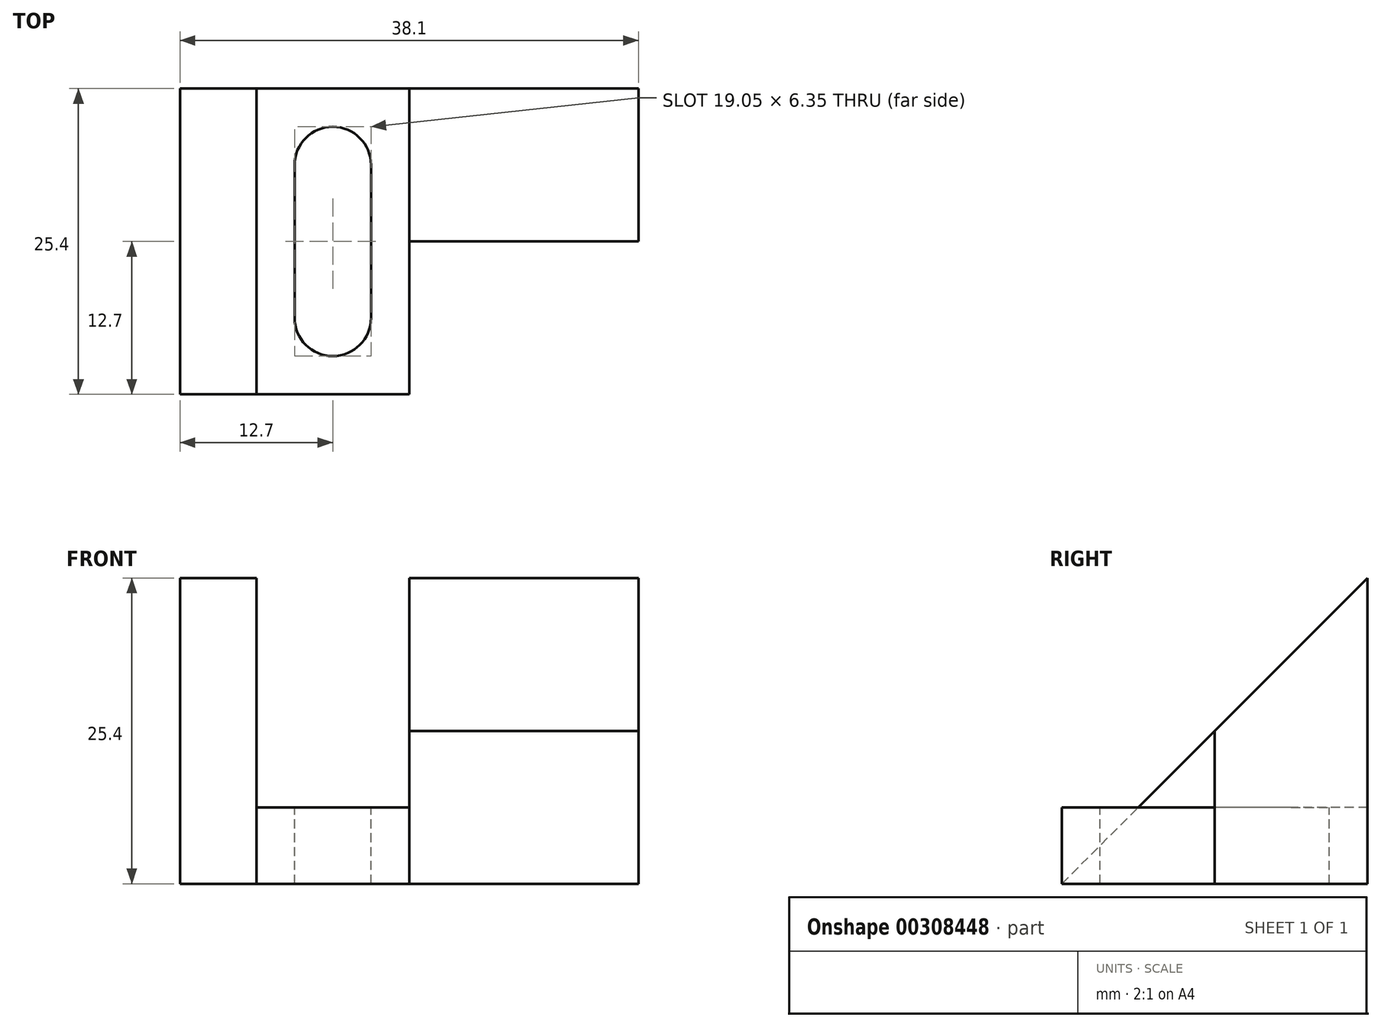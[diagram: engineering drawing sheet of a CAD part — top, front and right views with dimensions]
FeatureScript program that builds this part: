
annotation { "Feature Type Name" : "Feature", "Feature Type Description" : "" }
export const myFeature = defineFeature(function(context is Context, id is Id, definition is map)
    precondition{}
    {
        {
            var Q0;
            Q0=qCreatedBy(makeId("Right.planeOp"),FACE);
            var sketch = newSketch(context, id + "F0", { "sketchPlane" : qUnion([Q0])});
            skLineSegment(sketch, "E0", {"start": v(0, 0) * mm, "end": v(25.4, 25.4) * mm});
            skLineSegment(sketch, "E1", {"start": v(25.4, 25.4) * mm, "end": v(25.4, 0) * mm});
            skLineSegment(sketch, "E2", {"start": v(25.4, 0) * mm, "end": v(0, 0) * mm});
            skLineSegment(sketch, "E3", {"start": v(25.4, 6.35) * mm, "end": v(0, 6.35) * mm});
            skLineSegment(sketch, "E4", {"start": v(0, 6.35) * mm, "end": v(0, 0) * mm});
            skLineSegment(sketch, "E5", {"start": v(12.7, 12.7) * mm, "end": v(12.7, 0) * mm});
            skSolve(sketch);
        }
        {
            var Q0;
            {var subQ0=sQuery(id+"F0.wireOp",EDGE,"E1");var subQ1=sQuery(id+"F0.wireOp",EDGE,"E0");var subQ2=makeQuery(id+"F0.imprint","INTERSECT",VERTEX,{"derivedFrom":[subQ1,subQ0]});Q0=makeQuery(id+"F0.imprint","IMPRINT",FACE,{"disambiguationData":[TD([[makeQuery(id+"F0.imprint","IMPRINT",EDGE,{"disambiguationData":[TD([[subQ2,1.0]])],"derivedFrom":subQ1}),-1.0]])]});}
            var Q1;
            {var subQ0=sQuery(id+"F0.wireOp",EDGE,"E2");Q1=makeQuery(id+"F0.imprint","IMPRINT",FACE,{"disambiguationData":[TD([[makeQuery(id+"F0.imprint","IMPRINT",EDGE,{"derivedFrom":subQ0}),-1.0]])]});}
            var Q2;
            {var subQ0=sQuery(id+"F0.wireOp",EDGE,"E5");var subQ1=sQuery(id+"F0.wireOp",EDGE,"E0");var subQ2=makeQuery(id+"F0.imprint","INTERSECT",VERTEX,{"derivedFrom":[subQ1,subQ0]});Q2=makeQuery(id+"F0.imprint","IMPRINT",FACE,{"disambiguationData":[TD([[makeQuery(id+"F0.imprint","IMPRINT",EDGE,{"disambiguationData":[TD([[subQ2,1.0]])],"derivedFrom":subQ1}),-1.0]])]});}
            extrude(context, id + "F1", {"entities" : qUnion([Q0, Q1, Q2]), "depth" : 6.35 * mm});
        }
        {
            var Q0;
            Q0=makeQuery(id+"F1.opExtrude","CAP_FACE",FACE,{"disambiguationData":[OSD([sQuery(id+"F0.wireOp",EDGE,"E0"),sQuery(id+"F0.wireOp",EDGE,"E1"),sQuery(id+"F0.wireOp",EDGE,"E2")])],"isStart":false});
            var sketch = newSketch(context, id + "F2", { "sketchPlane" : qUnion([Q0])});
            skLineSegment(sketch, "E6.0", {"start": v(25.4, 25.4) * mm, "end": v(25.4, 0) * mm});
            skLineSegment(sketch, "E7.0", {"start": v(25.4, 6.35) * mm, "end": v(0, 6.35) * mm});
            skLineSegment(sketch, "E8.0", {"start": v(0, 6.35) * mm, "end": v(0, 0) * mm});
            skLineSegment(sketch, "E9.0", {"start": v(25.4, 0) * mm, "end": v(0, 0) * mm});
            skSolve(sketch);
        }
        {
            var Q0;
            Q0 = qSketchRegion(id + "F2", true);
            extrude(context, id + "F3", {"entities" : qUnion([Q0]), "operationType" : NewBodyOperationType.ADD, "depth" : 12.7 * mm});
        }
        {
            var Q0;
            Q0=makeQuery(id+"F3.opExtrude","CAP_FACE",FACE,{"disambiguationData":[OSD([sQuery(id+"F2.wireOp",EDGE,"E6.0"),sQuery(id+"F2.wireOp",EDGE,"E7.0"),sQuery(id+"F2.wireOp",EDGE,"E8.0"),sQuery(id+"F2.wireOp",EDGE,"E9.0")])],"isStart":false});
            var sketch = newSketch(context, id + "F4", { "sketchPlane" : qUnion([Q0])});
            skLineSegment(sketch, "E10.0", {"start": v(12.7, 12.7) * mm, "end": v(12.7, 0) * mm});
            skLineSegment(sketch, "E11.0", {"start": v(25.4, 25.4) * mm, "end": v(25.4, 0) * mm});
            skLineSegment(sketch, "E12", {"start": v(25.4, 25.4) * mm, "end": v(12.7, 12.7) * mm});
            skLineSegment(sketch, "E13", {"start": v(12.7, 0) * mm, "end": v(25.4, 0) * mm});
            skSolve(sketch);
        }
        {
            var Q0;
            Q0 = qSketchRegion(id + "F4", true);
            extrude(context, id + "F5", {"entities" : qUnion([Q0]), "operationType" : NewBodyOperationType.ADD, "depth" : 19.05 * mm});
        }
        {
            var Q0;
            Q0=makeQuery(id+"F3.opExtrude","SWEPT_FACE",FACE,{"disambiguationData":[OSD([sQuery(id+"F2.wireOp",EDGE,"E7.0")])]});
            var sketch = newSketch(context, id + "F6", { "sketchPlane" : qUnion([Q0])});
            skLineSegment(sketch, "E14", {"start": v(12.7, 19.05) * mm, "end": v(12.7, 6.35) * mm, "construction": true});
            skPoint(sketch, "E14.startSnap0", {"position": v(19.05, 19.05) * mm});
            skPoint(sketch, "E14.startSnap1", {"position": v(12.7, 25.4) * mm});
            skPoint(sketch, "E14.endSnap0", {"position": v(12.7, 0) * mm});
            skArc(sketch, "E15.0.startCap", {"start": v(9.53, 19.05) * mm, "mid": v(12.7, 22.23) * mm, "end": v(15.88, 19.05) * mm});
            skArc(sketch, "E15.0.endCap", {"start": v(15.88, 6.35) * mm, "mid": v(12.7, 3.18) * mm, "end": v(9.53, 6.35) * mm});
            skLineSegment(sketch, "E15.0.left", {"start": v(15.88, 19.05) * mm, "end": v(15.88, 6.35) * mm});
            skLineSegment(sketch, "E15.0.right", {"start": v(9.53, 19.05) * mm, "end": v(9.53, 6.35) * mm});
            skSolve(sketch);
        }
        {
            var Q0;
            Q0 = qSketchRegion(id + "F6", true);
            extrude(context, id + "F7", {"entities" : qUnion([Q0]), "operationType" : NewBodyOperationType.REMOVE, "endBound" : BoundingType.THROUGH_ALL, "oppositeDirection" : true, "depth" : 25.4 * mm});
        }
    });
